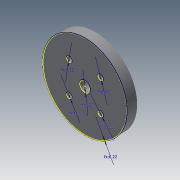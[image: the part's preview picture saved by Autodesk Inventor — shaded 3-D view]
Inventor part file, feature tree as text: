
AUTODESK INVENTOR PART (.ipt)
format: ipt  version: 2015 (Build 190159000, 159)  size: 108,544 bytes
history: native  units: mm
features: other x7, sketch x2, extrude x1, projected_geometry x1
ambient origin geometry x8: Origin, YZ Plane, XZ Plane, XY Plane, X Axis, Y Axis, Z Axis, Center Point
bodies: Body1 (feature_tree)
feature tree (11):
  other  "Blocks"
  extrude  "Extrusion3"  Depth=10.0mm
  sketch  "Sketch6"  dims[d6=5.0mm d7=15.0mm d8=15.0mm d9=10.0mm d10=0.0mm]
  other  "DXF"
  sketch  "Sketch1"  dims[d0=80.0mm d3=10.0mm]
  other  "Block1"
  other  "Block2"
  projected_geometry  "Projected Loop3"
  other  "Block3"
  other  "Block3:1"
  other  "Block3:2"
